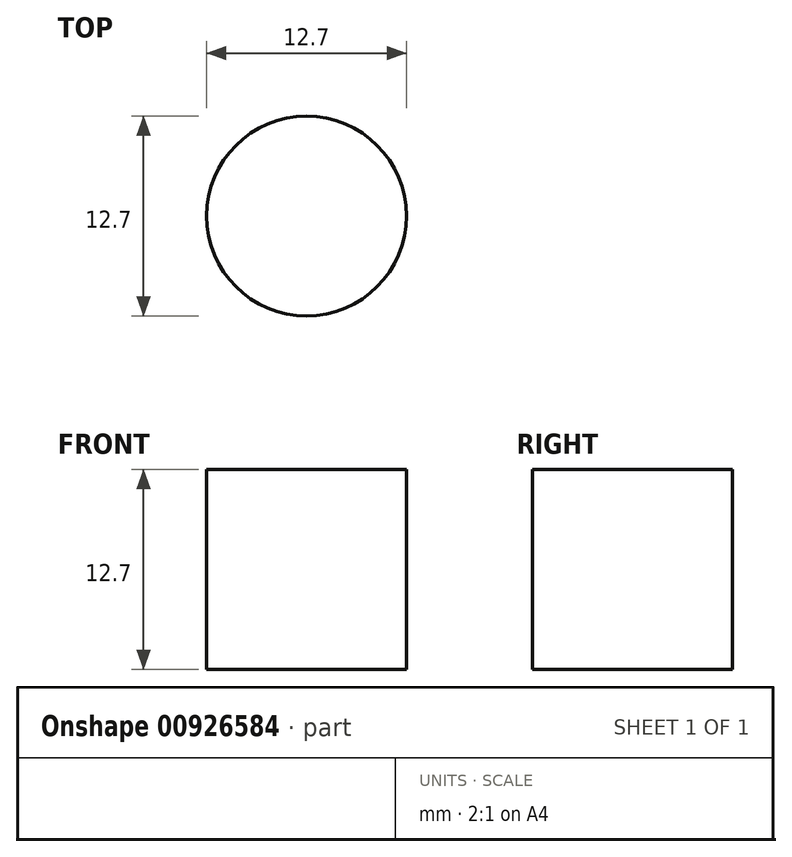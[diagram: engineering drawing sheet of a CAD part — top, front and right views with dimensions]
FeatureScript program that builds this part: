
annotation { "Feature Type Name" : "Feature", "Feature Type Description" : "" }
export const myFeature = defineFeature(function(context is Context, id is Id, definition is map)
    precondition{}
    {
        {
            var Q0;
            Q0=qCreatedBy(makeId("Top.planeOp"),FACE);
            var sketch = newSketch(context, id + "F0", { "sketchPlane" : qUnion([Q0])});
            skCircle(sketch, "E0", {"center": v(0, 0) * mm, "radius": 6.35 * mm});
            skSolve(sketch);
        }
        {
            var Q0;
            Q0=makeQuery(id+"F0.imprint","IMPRINT",FACE,{"disambiguationData":[TD([[makeQuery(id+"F0.imprint","IMPRINT",EDGE,{"derivedFrom":sQuery(id+"F0.wireOp",EDGE,"E0")}),1.0]])]});
            extrude(context, id + "F1", {"entities" : qUnion([Q0]), "depth" : 12.7 * mm, "offsetDistance" : 25.4 * mm});
        }
    });
